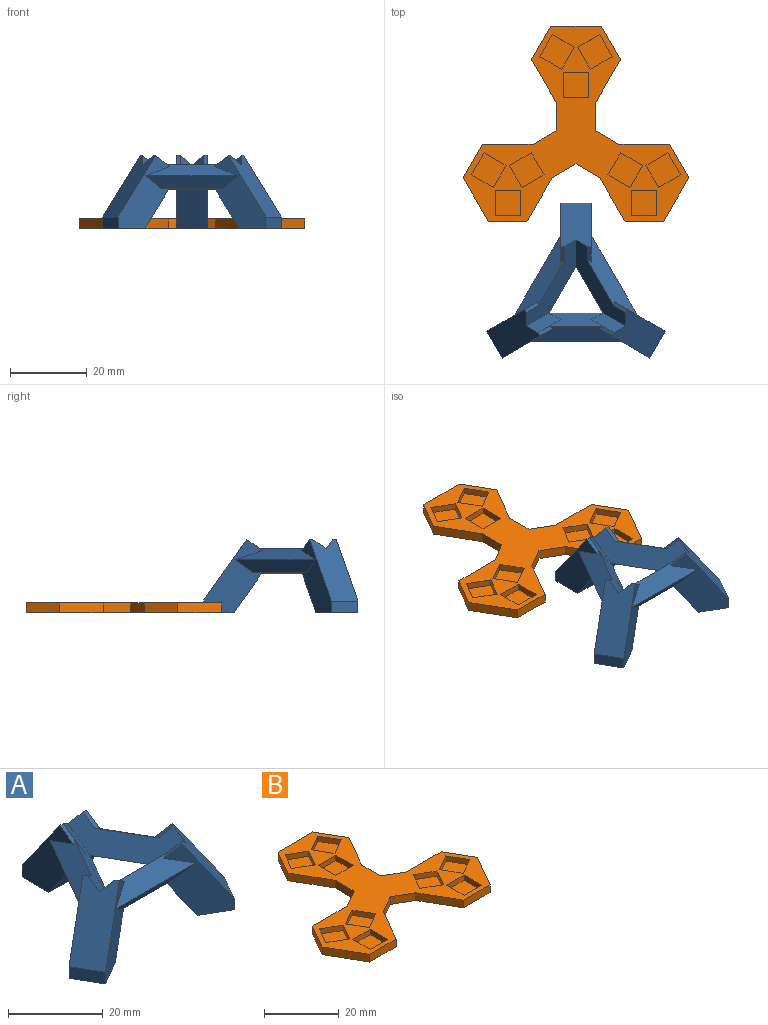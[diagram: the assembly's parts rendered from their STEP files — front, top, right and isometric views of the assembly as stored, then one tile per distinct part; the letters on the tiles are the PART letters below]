
ASSEMBLY  parts=2 mates=1
PART A: 61 faces, bbox 46.4x40.2x19 mm
  f0: plane 5.72x3.3mm, normal (-0.5,-0.87,0), area 13.2mm2, adj f1,f3,f4,f20
  f1: plane 5.72x3.3mm, normal (-0.87,0.5,0), area 13.2mm2, adj f0,f2,f4,f20
  f2: plane 5.72x3.3mm, normal (0.5,0.87,0), area 13.2mm2, adj f1,f3,f4,f20
  f3: plane 5.72x3.3mm, normal (0.87,-0.5,0), area 13.2mm2, adj f0,f2,f4,f20
  f4: plane 9.02x9.02mm, normal (0,0,-1), area 43.6mm2, adj f0,f1,f2,f3
  f5: plane 5.72x3.3mm, normal (-0.5,0.87,0), area 13.2mm2, adj f6,f8,f9,f41
  f6: plane 5.72x3.3mm, normal (0.87,0.5,0), area 13.2mm2, adj f5,f7,f9,f41
  f7: plane 5.72x3.3mm, normal (0.5,-0.87,0), area 13.2mm2, adj f6,f8,f9,f41
  f8: plane 5.72x3.3mm, normal (-0.87,-0.5,0), area 13.2mm2, adj f5,f7,f9,f41
  f9: plane 9.02x9.02mm, normal (0,0,-1), area 43.6mm2, adj f5,f6,f7,f8
  f10: plane 16x13.8mm, normal (0.71,-0.41,0.58), area 147.8mm2, adj f11,f12,f21,f22,f23,f28,f55
  f11: plane 3.5x2.89mm, normal (-0.5,0.29,0.82), area 4.6mm2, adj f10,f23,f24,f28
  f12: plane 4x2.86mm, normal (-0.5,0.29,0.82), area 4.6mm2, adj f10,f22,f29,f55
  f13: plane 16x11.31mm, normal (0,0.82,0.58), area 147.8mm2, adj f14,f15,f28,f32,f33,f34,f54
  f14: plane 4.04x2.86mm, normal (0,-0.58,0.82), area 4.6mm2, adj f13,f24,f28,f33
  f15: plane 4.04x2.86mm, normal (0,-0.58,0.82), area 4.6mm2, adj f13,f34,f35,f54
  f16: plane 16x13.8mm, normal (-0.71,-0.41,0.58), area 147.8mm2, adj f17,f18,f42,f43,f44,f52,f53
  f17: plane 3.5x2.89mm, normal (0.5,0.29,0.82), area 4.6mm2, adj f16,f35,f43,f53
  f18: plane 4x2.86mm, normal (0.5,0.29,0.82), area 4.6mm2, adj f16,f29,f44,f52
  f19: plane 11.78x10.57mm, normal (-0.71,0.41,-0.58), area 103.5mm2, adj f20,f22,f23,f25,f46,f49,f50
  f20: plane 10.93x10.93mm, normal (0,0,-1), area 20.4mm2, adj f0,f1,f2,f3,f19,f21,f22,f23
  f21: plane 6.93x4mm, normal (0.87,-0.5,0), area 24mm2, adj f10,f20,f22,f23
  f22: plane 19x13.3mm, normal (-0.5,-0.87,0), area 133.2mm2, adj f10,f12,f19,f20,f21,f29,f47,f50
  f23: plane 19x13.3mm, normal (0.5,0.87,0), area 133.2mm2, adj f10,f11,f19,f20,f21,f24,f27,f49
  f24: plane 20.77x12.99mm, normal (0.5,0.29,0.82), area 86mm2, adj f11,f14,f23,f27,f28,f33
  f25: plane 2.12x1.73mm, normal (0,-0.82,-0.58), area 0mm2, adj f19,f26
  f26: plane 13.48x9.2mm, normal (-0.5,-0.29,-0.82), area 42.5mm2, adj f25,f28,f30,f49
  f27: plane 20.77x11.99mm, normal (0.71,0.41,-0.58), area 77.4mm2, adj f23,f24,f33,f49
  f28: plane 22.38x12.92mm, normal (-0.71,-0.41,0.58), area 134.9mm2, adj f10,f11,f13,f14,f24,f26,f54,f55
  f29: plane 23.98x4.08mm, normal (0,-0.58,0.82), area 86mm2, adj f12,f18,f22,f44,f47,f48
  f30: plane 11.78x8.33mm, normal (0,-0.82,-0.58), area 103.5mm2, adj f26,f31,f33,f34,f36,f49,f51
  f31: plane 8x8mm, normal (0,0,-1), area 20.4mm2, adj f30,f32,f33,f34,f56,f57,f58,f59
  f32: plane 8x3mm, normal (0,1,0), area 24mm2, adj f13,f31,f33,f34
  f33: plane 19x15.35mm, normal (1,0,0), area 133.2mm2, adj f13,f14,f24,f27,f30,f31,f32,f49
  f34: plane 19x15.36mm, normal (-1,0,0), area 133.2mm2, adj f13,f15,f30,f31,f32,f35,f38,f51
  f35: plane 20.77x12.99mm, normal (-0.5,0.29,0.82), area 86mm2, adj f15,f17,f34,f38,f39,f43
  f36: plane 2.12x1.73mm, normal (0.71,0.41,-0.58), area 0mm2, adj f30,f37
  f37: plane 13.48x9.2mm, normal (0.5,-0.29,-0.82), area 42.5mm2, adj f36,f39,f40,f51
  f38: plane 20.77x11.99mm, normal (-0.71,0.41,-0.58), area 77.4mm2, adj f34,f35,f43,f51
  f39: plane 13.81x9.92mm, normal (0.71,-0.41,0.58), area 64.7mm2, adj f35,f37,f53,f54
  f40: plane 11.78x10.57mm, normal (0.71,0.41,-0.58), area 103.5mm2, adj f37,f41,f43,f44,f45,f50,f51
  f41: plane 10.93x10.93mm, normal (0,0,-1), area 20.4mm2, adj f5,f6,f7,f8,f40,f42,f43,f44
  f42: plane 6.93x4mm, normal (-0.87,-0.5,0), area 24mm2, adj f16,f41,f43,f44
  f43: plane 19x13.3mm, normal (-0.5,0.87,0), area 133.2mm2, adj f16,f17,f35,f38,f40,f41,f42,f51
  f44: plane 19x13.3mm, normal (0.5,-0.87,0), area 133.2mm2, adj f16,f18,f29,f40,f41,f42,f47,f50
  f45: plane 2.45x1.73mm, normal (-0.71,0.41,-0.58), area 0mm2, adj f40,f46
  f46: plane 14.15x2.45mm, normal (0,0.58,-0.82), area 42.5mm2, adj f19,f45,f48,f50
  f47: plane 23.98x3.14mm, normal (0,-0.82,-0.58), area 77.4mm2, adj f22,f29,f44,f50
  f48: plane 14.15x4.77mm, normal (0,0.82,0.58), area 64.7mm2, adj f29,f46,f52,f55
  f49: plane 14.58x10.03mm, normal (0.15,0.08,-0.99), area 38.3mm2, adj f19,f23,f26,f27,f30,f33
  f50: plane 16.3x2.79mm, normal (0,-0.17,-0.99), area 38.3mm2, adj f19,f22,f40,f44,f46,f47
  f51: plane 14.58x10.03mm, normal (-0.15,0.08,-0.99), area 38.3mm2, adj f30,f34,f37,f38,f40,f43
  f52: plane 8.84x7.22mm, normal (0,0.82,0.58), area 35.1mm2, adj f16,f18,f48,f53
  f53: plane 7.22x6.84mm, normal (0.71,-0.41,0.58), area 35.1mm2, adj f16,f17,f39,f52
  f54: plane 8.48x7.22mm, normal (0.71,-0.41,0.58), area 35.1mm2, adj f13,f15,f28,f39
  f55: plane 8.84x7.22mm, normal (0,0.82,0.58), area 35.1mm2, adj f10,f12,f28,f48
  f56: plane 6.6x2mm, normal (1,0,0), area 13.2mm2, adj f31,f57,f59,f60
  f57: plane 6.6x2mm, normal (0,-1,0), area 13.2mm2, adj f31,f56,f58,f60
  f58: plane 6.6x2mm, normal (-1,0,0), area 13.2mm2, adj f31,f57,f59,f60
  f59: plane 6.6x2mm, normal (0,1,0), area 13.2mm2, adj f31,f56,f58,f60
  f60: plane 6.6x6.6mm, normal (0,0,-1), area 43.6mm2, adj f56,f57,f58,f59
PART B: 68 faces, bbox 58.7x50.8x2.5 mm
  f0: plane 7.11x2.5mm, normal (1,0,0), area 17.8mm2, adj f1,f3,f8,f26
  f1: plane 58.69x50.83mm, normal (0,0,1), area 905.6mm2, adj f0,f2,f3,f4,f5,f6,f7,f9
  f2: plane 7.11x2.5mm, normal (-1,0,0), area 17.8mm2, adj f1,f7,f8,f24
  f3: plane 11.42x6.59mm, normal (0.87,-0.5,0), area 33mm2, adj f0,f1,f4,f8
  f4: plane 8.66x5mm, normal (0.87,0.5,0), area 25mm2, adj f1,f3,f5,f8
  f5: plane 13.19x2.5mm, normal (0,1,0), area 33mm2, adj f1,f4,f6,f8
  f6: plane 8.66x5mm, normal (-0.87,0.5,0), area 25mm2, adj f1,f5,f7,f8
  f7: plane 11.42x6.59mm, normal (-0.87,-0.5,0), area 33mm2, adj f1,f2,f6,f8
  f8: plane 58.69x50.83mm, normal (0,0,-1), area 1297.7mm2, adj f0,f2,f3,f4,f5,f6,f7,f24
  f9: plane 5.72x3.3mm, normal (-0.5,-0.87,0), area 11.2mm2, adj f1,f10,f12,f13
  f10: plane 5.72x3.3mm, normal (0.87,-0.5,0), area 11.2mm2, adj f1,f9,f11,f13
  f11: plane 5.72x3.3mm, normal (0.5,0.87,0), area 11.2mm2, adj f1,f10,f12,f13
  f12: plane 5.72x3.3mm, normal (-0.87,0.5,0), area 11.2mm2, adj f1,f9,f11,f13
  f13: plane 9.02x9.02mm, normal (0,0,1), area 43.6mm2, adj f9,f10,f11,f12
  f14: plane 5.72x3.3mm, normal (-0.87,-0.5,0), area 11.2mm2, adj f1,f15,f17,f18
  f15: plane 5.72x3.3mm, normal (0.5,-0.87,0), area 11.2mm2, adj f1,f14,f16,f18
  f16: plane 5.72x3.3mm, normal (0.87,0.5,0), area 11.2mm2, adj f1,f15,f17,f18
  f17: plane 5.72x3.3mm, normal (-0.5,0.87,0), area 11.2mm2, adj f1,f14,f16,f18
  f18: plane 9.02x9.02mm, normal (0,0,1), area 43.6mm2, adj f14,f15,f16,f17
  f19: plane 6.6x1.7mm, normal (0,-1,0), area 11.2mm2, adj f1,f20,f22,f23
  f20: plane 6.6x1.7mm, normal (1,0,0), area 11.2mm2, adj f1,f19,f21,f23
  f21: plane 6.6x1.7mm, normal (0,1,0), area 11.2mm2, adj f1,f20,f22,f23
  f22: plane 6.6x1.7mm, normal (-1,0,0), area 11.2mm2, adj f1,f19,f21,f23
  f23: plane 6.6x6.6mm, normal (0,0,1), area 43.6mm2, adj f19,f20,f21,f22
  f24: plane 6.16x3.56mm, normal (-0.5,0.87,0), area 17.8mm2, adj f1,f2,f8,f48
  f25: plane 6.16x3.56mm, normal (-0.5,-0.87,0), area 17.8mm2, adj f1,f8,f27,f47
  f26: plane 6.16x3.56mm, normal (0.5,0.87,0), area 17.8mm2, adj f0,f1,f8,f31
  f27: plane 11.42x6.59mm, normal (-0.87,-0.5,0), area 33mm2, adj f1,f8,f25,f28
  f28: plane 10x2.5mm, normal (0,-1,0), area 25mm2, adj f1,f8,f27,f29
  f29: plane 11.42x6.59mm, normal (0.87,-0.5,0), area 33mm2, adj f1,f8,f28,f30
  f30: plane 8.66x5mm, normal (0.87,0.5,0), area 25mm2, adj f1,f8,f29,f31
  f31: plane 13.19x2.5mm, normal (0,1,0), area 33mm2, adj f1,f8,f26,f30
  f32: plane 5.72x3.3mm, normal (-0.5,0.87,0), area 11.2mm2, adj f1,f33,f35,f36
  f33: plane 5.72x3.3mm, normal (-0.87,-0.5,0), area 11.2mm2, adj f1,f32,f34,f36
  f34: plane 5.72x3.3mm, normal (0.5,-0.87,0), area 11.2mm2, adj f1,f33,f35,f36
  f35: plane 5.72x3.3mm, normal (0.87,0.5,0), area 11.2mm2, adj f1,f32,f34,f36
  f36: plane 9.02x9.02mm, normal (0,0,1), area 43.6mm2, adj f32,f33,f34,f35
  f37: plane 6.6x1.7mm, normal (0,1,0), area 11.2mm2, adj f1,f38,f40,f41
  f38: plane 6.6x1.7mm, normal (-1,0,0), area 11.2mm2, adj f1,f37,f39,f41
  f39: plane 6.6x1.7mm, normal (0,-1,0), area 11.2mm2, adj f1,f38,f40,f41
  f40: plane 6.6x1.7mm, normal (1,0,0), area 11.2mm2, adj f1,f37,f39,f41
  f41: plane 6.6x6.6mm, normal (0,0,1), area 43.6mm2, adj f37,f38,f39,f40
  f42: plane 5.72x3.3mm, normal (-0.87,0.5,0), area 11.2mm2, adj f1,f43,f45,f46
  f43: plane 5.72x3.3mm, normal (-0.5,-0.87,0), area 11.2mm2, adj f1,f42,f44,f46
  f44: plane 5.72x3.3mm, normal (0.87,-0.5,0), area 11.2mm2, adj f1,f43,f45,f46
  f45: plane 5.72x3.3mm, normal (0.5,0.87,0), area 11.2mm2, adj f1,f42,f44,f46
  f46: plane 9.02x9.02mm, normal (0,0,1), area 43.6mm2, adj f42,f43,f44,f45
  f47: plane 6.16x3.56mm, normal (0.5,-0.87,0), area 17.8mm2, adj f1,f8,f25,f52
  f48: plane 13.19x2.5mm, normal (0,1,0), area 33mm2, adj f1,f8,f24,f49
  f49: plane 8.66x5mm, normal (-0.87,0.5,0), area 25mm2, adj f1,f8,f48,f50
  f50: plane 11.42x6.59mm, normal (-0.87,-0.5,0), area 33mm2, adj f1,f8,f49,f51
  f51: plane 10x2.5mm, normal (0,-1,0), area 25mm2, adj f1,f8,f50,f52
  f52: plane 11.42x6.59mm, normal (0.87,-0.5,0), area 33mm2, adj f1,f8,f47,f51
  f53: plane 6.6x1.7mm, normal (1,0,0), area 11.2mm2, adj f1,f54,f56,f57
  f54: plane 6.6x1.7mm, normal (0,1,0), area 11.2mm2, adj f1,f53,f55,f57
  f55: plane 6.6x1.7mm, normal (-1,0,0), area 11.2mm2, adj f1,f54,f56,f57
  f56: plane 6.6x1.7mm, normal (0,-1,0), area 11.2mm2, adj f1,f53,f55,f57
  f57: plane 6.6x6.6mm, normal (0,0,1), area 43.6mm2, adj f53,f54,f55,f56
  f58: plane 5.72x3.3mm, normal (0.87,-0.5,0), area 11.2mm2, adj f1,f59,f61,f62
  f59: plane 5.72x3.3mm, normal (0.5,0.87,0), area 11.2mm2, adj f1,f58,f60,f62
  f60: plane 5.72x3.3mm, normal (-0.87,0.5,0), area 11.2mm2, adj f1,f59,f61,f62
  f61: plane 5.72x3.3mm, normal (-0.5,-0.87,0), area 11.2mm2, adj f1,f58,f60,f62
  f62: plane 9.02x9.02mm, normal (0,0,1), area 43.6mm2, adj f58,f59,f60,f61
  f63: plane 5.72x3.3mm, normal (0.87,0.5,0), area 11.2mm2, adj f1,f64,f66,f67
  f64: plane 5.72x3.3mm, normal (-0.5,0.87,0), area 11.2mm2, adj f1,f63,f65,f67
  f65: plane 5.72x3.3mm, normal (-0.87,-0.5,0), area 11.2mm2, adj f1,f64,f66,f67
  f66: plane 5.72x3.3mm, normal (0.5,-0.87,0), area 11.2mm2, adj f1,f63,f65,f67
  f67: plane 9.02x9.02mm, normal (0,0,1), area 43.6mm2, adj f63,f64,f65,f66
PLACE A t=(0,-40.5,-4)mm
PLACE B t=(0,0,2.5)mm
MATE fastened B.f8 <-> A.f31  axis (0,0,-1) through (0,0,0)mm
